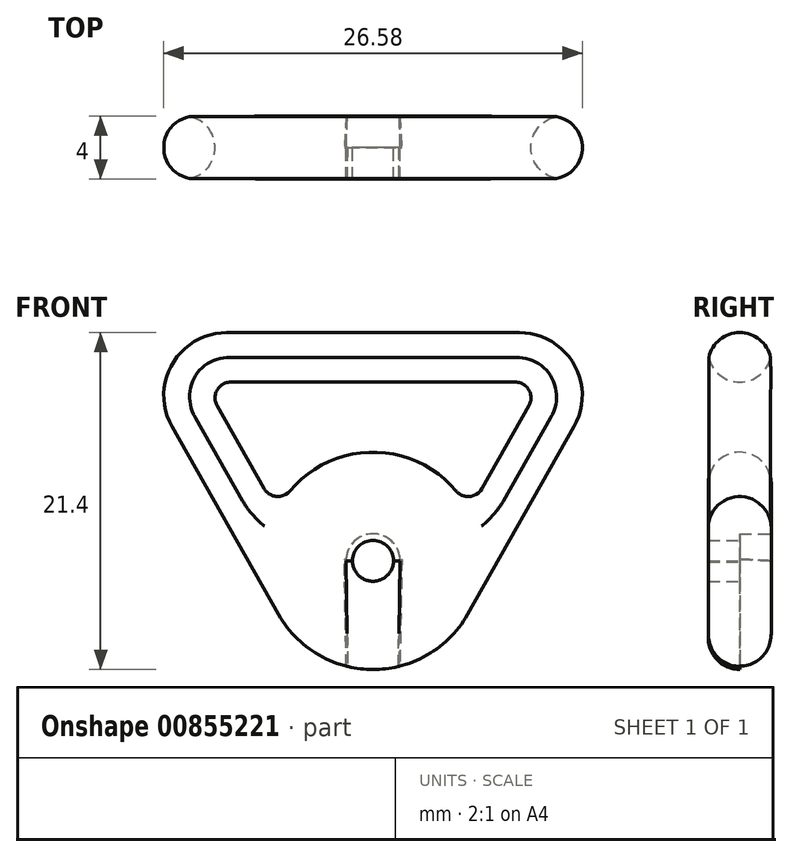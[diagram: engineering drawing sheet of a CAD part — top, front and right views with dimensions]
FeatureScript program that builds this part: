
annotation { "Feature Type Name" : "Feature", "Feature Type Description" : "" }
export const myFeature = defineFeature(function(context is Context, id is Id, definition is map)
    precondition{}
    {
        {
            var Q0;
            Q0=qCreatedBy(makeId("Front.planeOp"),FACE);
            var sketch = newSketch(context, id + "F0", { "sketchPlane" : qUnion([Q0])});
            skCircle(sketch, "E0", {"center": v(0, 0) * mm, "radius": 1.72 * mm});
            skArc(sketch, "E1", {"start": v(-6, -3.4) * mm, "mid": v(0, -6.9) * mm, "end": v(6, -3.4) * mm});
            skLineSegment(sketch, "E2", {"start": v(-9.03, 11.35) * mm, "end": v(9.03, 11.35) * mm});
            skLineSegment(sketch, "E3", {"start": v(9.9, 9.86) * mm, "end": v(6.92, 4.6) * mm});
            skLineSegment(sketch, "E4", {"start": v(-9.9, 9.86) * mm, "end": v(-6.92, 4.6) * mm});
            skLineSegment(sketch, "E5", {"start": v(-9.3, 14.5) * mm, "end": v(9.3, 14.5) * mm});
            skLineSegment(sketch, "E6", {"start": v(12.77, 8.53) * mm, "end": v(6, -3.4) * mm});
            skLineSegment(sketch, "E7", {"start": v(-12.77, 8.53) * mm, "end": v(-6, -3.4) * mm});
            skLineSegment(sketch, "E8", {"start": v(0, 0) * mm, "end": v(0, 11.35) * mm, "construction": true});
            skLineSegment(sketch, "E9", {"start": v(-17.36, -6.9) * mm, "end": v(5.43, -6.9) * mm, "construction": true});
            skPoint(sketch, "E10.visualSharp", {"position": v(-16.16, 14.5) * mm});
            skArc(sketch, "E10.filletArc", {"start": v(-9.3, 14.5) * mm, "mid": v(-12.75, 12.51) * mm, "end": v(-12.77, 8.53) * mm});
            skPoint(sketch, "E11.visualSharp", {"position": v(16.16, 14.5) * mm});
            skArc(sketch, "E11.filletArc", {"start": v(12.77, 8.53) * mm, "mid": v(12.75, 12.51) * mm, "end": v(9.3, 14.5) * mm});
            skArc(sketch, "E12.trimOffspring", {"start": v(5.28, 4.44) * mm, "mid": v(0, 6.9) * mm, "end": v(-5.28, 4.44) * mm});
            skPoint(sketch, "E13.visualSharp", {"position": v(-6.12, 3.19) * mm});
            skArc(sketch, "E13.filletArc", {"start": v(-6.92, 4.6) * mm, "mid": v(-6.14, 4.09) * mm, "end": v(-5.28, 4.44) * mm});
            skPoint(sketch, "E14.visualSharp", {"position": v(6.12, 3.19) * mm});
            skArc(sketch, "E14.filletArc", {"start": v(5.28, 4.44) * mm, "mid": v(6.14, 4.09) * mm, "end": v(6.92, 4.6) * mm});
            skPoint(sketch, "E15.visualSharp", {"position": v(-10.75, 11.35) * mm});
            skArc(sketch, "E15.filletArc", {"start": v(-9.03, 11.35) * mm, "mid": v(-9.9, 10.85) * mm, "end": v(-9.9, 9.86) * mm});
            skPoint(sketch, "E16.visualSharp", {"position": v(10.75, 11.35) * mm});
            skArc(sketch, "E16.filletArc", {"start": v(9.9, 9.86) * mm, "mid": v(9.9, 10.85) * mm, "end": v(9.03, 11.35) * mm});
            skCircle(sketch, "E17", {"center": v(0, 0) * mm, "radius": 1.3 * mm});
            skLineSegment(sketch, "E18", {"start": v(1.72, 0) * mm, "end": v(1.6, -6.9) * mm});
            skLineSegment(sketch, "E19", {"start": v(-1.72, 0) * mm, "end": v(-1.6, -6.9) * mm});
            skLineSegment(sketch, "E20", {"start": v(1.72, 0) * mm, "end": v(1.3, 0) * mm});
            skLineSegment(sketch, "E21", {"start": v(-1.72, 0) * mm, "end": v(-1.3, 0) * mm});
            skSolve(sketch);
        }
        {
            var Q0;
            {var subQ3=sQuery(id+"F0.wireOp",EDGE,"E19");var subQ5=sQuery(id+"F0.wireOp",EDGE,"E1");var subQ6=makeQuery(id+"F0.imprint","INTERSECT",VERTEX,{"derivedFrom":[subQ5,subQ3]});Q0=makeQuery(id+"F0.imprint","IMPRINT",FACE,{"disambiguationData":[TD([[makeQuery(id+"F0.imprint","IMPRINT",EDGE,{"disambiguationData":[TD([[subQ6,-1.0]])],"derivedFrom":subQ5}),1.0]])]});}
            var Q1;
            {var subQ0=sQuery(id+"F0.wireOp",EDGE,"E20");Q1=makeQuery(id+"F0.imprint","IMPRINT",FACE,{"disambiguationData":[TD([[makeQuery(id+"F0.imprint","IMPRINT",EDGE,{"derivedFrom":subQ0}),1.0]])]});}
            extrude(context, id + "F1", {"entities" : qUnion([Q0, Q1]), "depth" : 2 * mm, "offsetDistance" : 25 * mm, "hasDraft" : true, "draftAngle" : 3 * degree});
        }
        {
            var Q0;
            {var subQ0=sQuery(id+"F0.wireOp",EDGE,"E20");Q0=makeQuery(id+"F0.imprint","IMPRINT",FACE,{"disambiguationData":[TD([[makeQuery(id+"F0.imprint","IMPRINT",EDGE,{"derivedFrom":subQ0}),1.0]])]});}
            var Q1;
            {var subQ3=sQuery(id+"F0.wireOp",EDGE,"E19");var subQ5=sQuery(id+"F0.wireOp",EDGE,"E1");var subQ6=makeQuery(id+"F0.imprint","INTERSECT",VERTEX,{"derivedFrom":[subQ5,subQ3]});Q1=makeQuery(id+"F0.imprint","IMPRINT",FACE,{"disambiguationData":[TD([[makeQuery(id+"F0.imprint","IMPRINT",EDGE,{"disambiguationData":[TD([[subQ6,-1.0]])],"derivedFrom":subQ5}),1.0]])]});}
            extrude(context, id + "F2", {"entities" : qUnion([Q0, Q1]), "operationType" : NewBodyOperationType.ADD, "depth" : 4 * mm, "offsetDistance" : 25 * mm});
        }
        {
            var Q0;
            Q0=makeQuery(id+"F1.opExtrude","CAP_FACE",FACE,{"disambiguationData":[OSD([sQuery(id+"F0.wireOp",EDGE,"E1"),sQuery(id+"F0.wireOp",EDGE,"E2"),sQuery(id+"F0.wireOp",EDGE,"E3"),sQuery(id+"F0.wireOp",EDGE,"E4"),sQuery(id+"F0.wireOp",EDGE,"E5"),sQuery(id+"F0.wireOp",EDGE,"E6"),sQuery(id+"F0.wireOp",EDGE,"E7"),sQuery(id+"F0.wireOp",EDGE,"E10.filletArc"),sQuery(id+"F0.wireOp",EDGE,"E11.filletArc"),sQuery(id+"F0.wireOp",EDGE,"E12.trimOffspring"),sQuery(id+"F0.wireOp",EDGE,"E13.filletArc"),sQuery(id+"F0.wireOp",EDGE,"E14.filletArc"),sQuery(id+"F0.wireOp",EDGE,"E15.filletArc"),sQuery(id+"F0.wireOp",EDGE,"E16.filletArc"),sQuery(id+"F0.wireOp",EDGE,"E17")])],"isStart":false});
            cPlane(context, id + "F3", {"entities" : qUnion([Q0]), "cplaneType" : CPlaneType.OFFSET, "offset" : 0 * mm, "width" : 150 * mm, "height" : 150 * mm});
        }
        {
            var Q0;
            Q0=makeQuery(id+"F0.imprint","IMPRINT",FACE,{"disambiguationData":[TD([[makeQuery(id+"F0.imprint","IMPRINT",EDGE,{"derivedFrom":sQuery(id+"F0.wireOp",EDGE,"E2")}),1.0]])]});
            var Q1;
            {var subQ0=sQuery(id+"F0.wireOp",EDGE,"E20");Q1=makeQuery(id+"F0.imprint","IMPRINT",FACE,{"disambiguationData":[TD([[makeQuery(id+"F0.imprint","IMPRINT",EDGE,{"derivedFrom":subQ0}),-1.0]])]});}
            extrude(context, id + "F4", {"entities" : qUnion([Q0, Q1]), "depth" : 4 * mm, "offsetDistance" : 25 * mm});
        }
        {
            var Q0;
            {var subQ3=sQuery(id+"F0.wireOp",EDGE,"E19");var subQ5=sQuery(id+"F0.wireOp",EDGE,"E1");var subQ6=makeQuery(id+"F0.imprint","INTERSECT",VERTEX,{"derivedFrom":[subQ5,subQ3]});Q0=makeQuery(id+"F0.imprint","IMPRINT",FACE,{"disambiguationData":[TD([[makeQuery(id+"F0.imprint","IMPRINT",EDGE,{"disambiguationData":[TD([[subQ6,-1.0]])],"derivedFrom":subQ5}),1.0]])]});}
            var Q1;
            {var subQ0=sQuery(id+"F0.wireOp",EDGE,"E20");Q1=makeQuery(id+"F0.imprint","IMPRINT",FACE,{"disambiguationData":[TD([[makeQuery(id+"F0.imprint","IMPRINT",EDGE,{"derivedFrom":subQ0}),1.0]])]});}
            extrude(context, id + "F5", {"entities" : qUnion([Q0, Q1]), "operationType" : NewBodyOperationType.REMOVE, "depth" : 2 * mm, "offsetDistance" : 25 * mm, "hasDraft" : true, "draftAngle" : 3 * degree});
        }
        {
            var Q0;
            {var subQ0=sQuery(id+"F0.wireOp",EDGE,"E20");Q0=makeQuery(id+"F0.imprint","IMPRINT",FACE,{"disambiguationData":[TD([[makeQuery(id+"F0.imprint","IMPRINT",EDGE,{"derivedFrom":subQ0}),-1.0]])]});}
            extrude(context, id + "F6", {"entities" : qUnion([Q0]), "operationType" : NewBodyOperationType.REMOVE, "depth" : 2 * mm, "offsetDistance" : 25 * mm});
        }
        {
            var Q0;
            {var subQ2=sQuery(id+"F0.wireOp",EDGE,"E20");Q0=makeQuery(id+"F0.imprint","IMPRINT",FACE,{"disambiguationData":[TD([[makeQuery(id+"F0.imprint","IMPRINT",EDGE,{"derivedFrom":subQ2}),1.0]])]});}
            extrude(context, id + "F7", {"entities" : qUnion([Q0]), "operationType" : NewBodyOperationType.REMOVE, "depth" : 2 * mm, "offsetDistance" : 25 * mm, "hasDraft" : true, "draftAngle" : 3 * degree});
        }
        {
            var Q0;
            Q0=makeQuery(id+"F4.opExtrude","CAP_EDGE",EDGE,{"disambiguationData":[OSD([sQuery(id+"F0.wireOp",EDGE,"E2")])],"isStart":false});
            var Q1;
            Q1=makeQuery(id+"F4.opExtrude","CAP_EDGE",EDGE,{"disambiguationData":[OSD([sQuery(id+"F0.wireOp",EDGE,"E2")])],"isStart":true});
            var Q2;
            Q2=makeQuery(id+"F4.opExtrude","CAP_EDGE",EDGE,{"disambiguationData":[OSD([sQuery(id+"F0.wireOp",EDGE,"E5")])],"isStart":true});
            var Q3;
            Q3=makeQuery(id+"F4.opExtrude","CAP_EDGE",EDGE,{"disambiguationData":[OSD([sQuery(id+"F0.wireOp",EDGE,"E7")])],"isStart":false});
            fillet(context, id + "F8", {"entities" : qUnion([Q0, Q1, Q2, Q3]), "radius" : 2 * mm, "tangentPropagation" : true, "allowEdgeOverflow" : false});
        }
        {
            var Q0;
            Q0=makeQuery(id+"F2.opExtrude","CAP_EDGE",EDGE,{"disambiguationData":[OSD([sQuery(id+"F0.wireOp",EDGE,"E1")])],"isStart":false});
            var Q1;
            Q1=makeQuery(id+"F1.opExtrude","CAP_EDGE",EDGE,{"disambiguationData":[OSD([sQuery(id+"F0.wireOp",EDGE,"E1")])],"isStart":true});
            fillet(context, id + "F9", {"entities" : qUnion([Q0, Q1]), "radius" : 2 * mm, "tangentPropagation" : true, "allowEdgeOverflow" : false});
        }
    });
